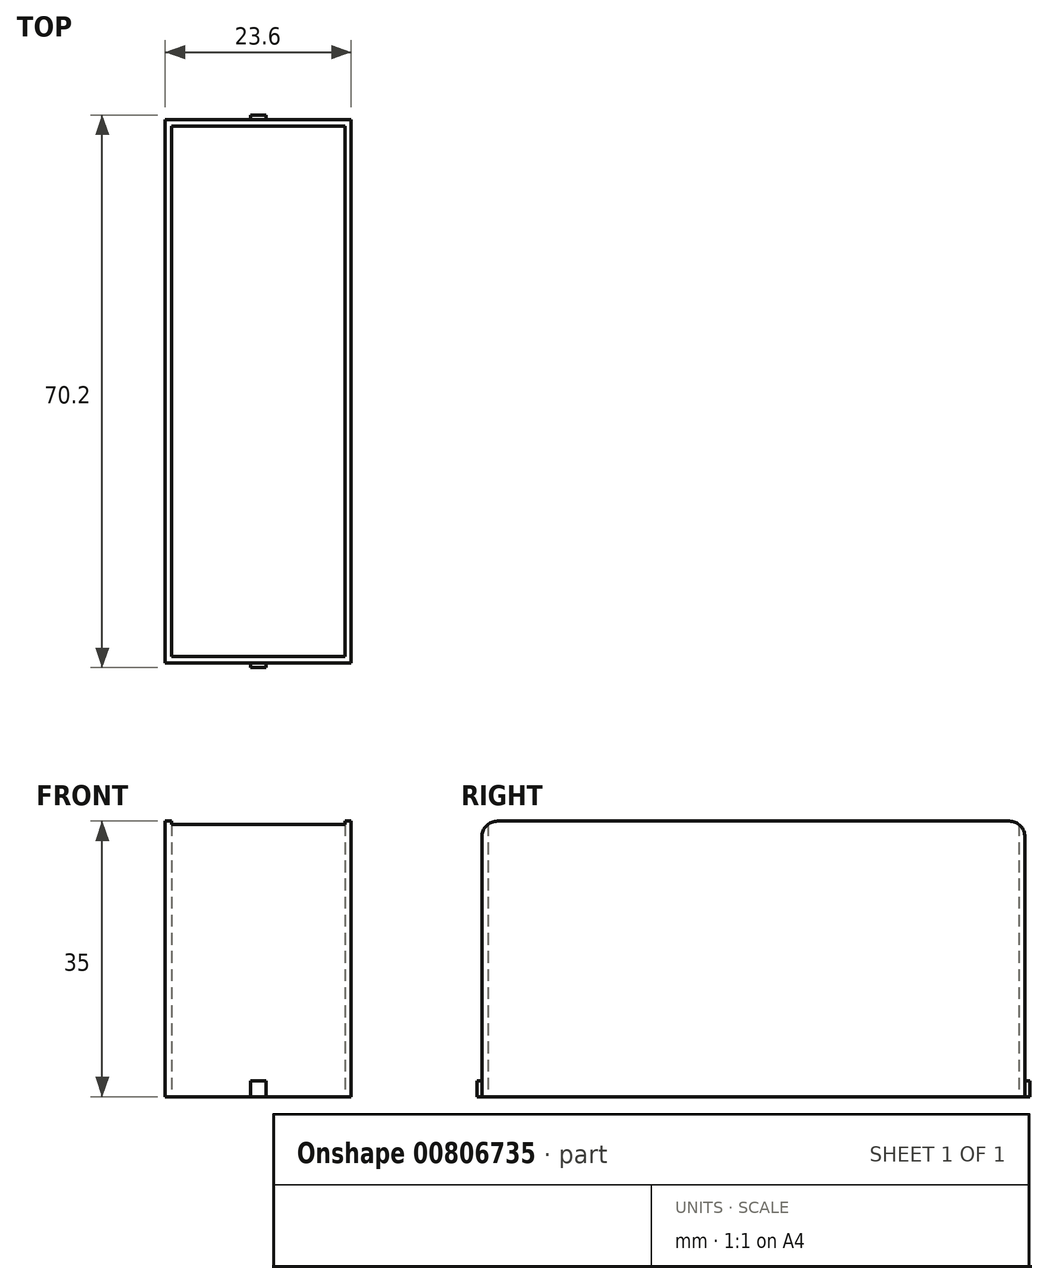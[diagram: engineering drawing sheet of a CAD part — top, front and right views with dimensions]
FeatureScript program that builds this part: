
annotation { "Feature Type Name" : "Feature", "Feature Type Description" : "" }
export const myFeature = defineFeature(function(context is Context, id is Id, definition is map)
    precondition{}
    {
        {
            var Q0;
            Q0=qCreatedBy(makeId("Top.planeOp"),FACE);
            var sketch = newSketch(context, id + "F0", { "sketchPlane" : qUnion([Q0])});
            skLineSegment(sketch, "E0.bottom", {"start": v(-11, 33.7) * mm, "end": v(11, 33.7) * mm});
            skLineSegment(sketch, "E0.top", {"start": v(-11, -33.7) * mm, "end": v(11, -33.7) * mm});
            skLineSegment(sketch, "E0.left", {"start": v(-11, 33.7) * mm, "end": v(-11, -33.7) * mm});
            skLineSegment(sketch, "E0.right", {"start": v(11, 33.7) * mm, "end": v(11, -33.7) * mm});
            skLineSegment(sketch, "E1.bottom", {"start": v(-11.8, 34.5) * mm, "end": v(11.8, 34.5) * mm});
            skLineSegment(sketch, "E1.top", {"start": v(-11.8, -34.5) * mm, "end": v(11.8, -34.5) * mm});
            skLineSegment(sketch, "E1.left", {"start": v(-11.8, 34.5) * mm, "end": v(-11.8, -34.5) * mm});
            skLineSegment(sketch, "E1.right", {"start": v(11.8, 34.5) * mm, "end": v(11.8, -34.5) * mm});
            skSolve(sketch);
        }
        {
            var Q0;
            Q0 = qSketchRegion(id + "F0", true);
            extrude(context, id + "F1", {"entities" : qUnion([Q0]), "depth" : 35 * mm, "offsetDistance" : 25 * mm});
        }
        {
            var Q0;
            Q0=makeQuery(id+"F1.opExtrude","CAP_EDGE",EDGE,{"disambiguationData":[OSD([sQuery(id+"F0.wireOp",EDGE,"E1.top")])],"isStart":false});
            var Q1;
            Q1=makeQuery(id+"F1.opExtrude","CAP_EDGE",EDGE,{"disambiguationData":[OSD([sQuery(id+"F0.wireOp",EDGE,"E1.bottom")])],"isStart":false});
            fillet(context, id + "F2", {"entities" : qUnion([Q0, Q1]), "radius" : 2 * mm, "tangentPropagation" : true, "allowEdgeOverflow" : false});
        }
        {
            var Q0;
            Q0=makeQuery(id+"F1.opExtrude","CAP_FACE",FACE,{"disambiguationData":[OSD([sQuery(id+"F0.wireOp",EDGE,"E0.bottom"),sQuery(id+"F0.wireOp",EDGE,"E0.top"),sQuery(id+"F0.wireOp",EDGE,"E0.left"),sQuery(id+"F0.wireOp",EDGE,"E0.right"),sQuery(id+"F0.wireOp",EDGE,"E1.bottom"),sQuery(id+"F0.wireOp",EDGE,"E1.top"),sQuery(id+"F0.wireOp",EDGE,"E1.left"),sQuery(id+"F0.wireOp",EDGE,"E1.right")])],"isStart":true});
            var sketch = newSketch(context, id + "F3", { "sketchPlane" : qUnion([Q0])});
            skLineSegment(sketch, "E2.bottom", {"start": v(-1, 35.1) * mm, "end": v(1, 35.1) * mm});
            skLineSegment(sketch, "E2.top", {"start": v(-1, 34.5) * mm, "end": v(1, 34.5) * mm});
            skLineSegment(sketch, "E2.left", {"start": v(-1, 35.1) * mm, "end": v(-1, 34.5) * mm});
            skLineSegment(sketch, "E2.right", {"start": v(1, 35.1) * mm, "end": v(1, 34.5) * mm});
            skLineSegment(sketch, "E3.bottom", {"start": v(-1, -35.1) * mm, "end": v(1, -35.1) * mm});
            skLineSegment(sketch, "E3.top", {"start": v(-1, -34.5) * mm, "end": v(1, -34.5) * mm});
            skLineSegment(sketch, "E3.left", {"start": v(-1, -35.1) * mm, "end": v(-1, -34.5) * mm});
            skLineSegment(sketch, "E3.right", {"start": v(1, -35.1) * mm, "end": v(1, -34.5) * mm});
            skSolve(sketch);
        }
        {
            var Q0;
            Q0=makeQuery(id+"F3.imprint","IMPRINT",FACE,{"disambiguationData":[TD([[makeQuery(id+"F3.imprint","IMPRINT",EDGE,{"derivedFrom":sQuery(id+"F3.wireOp",EDGE,"E2.bottom")}),-1.0]])]});
            var Q1;
            Q1=makeQuery(id+"F3.imprint","IMPRINT",FACE,{"disambiguationData":[TD([[makeQuery(id+"F3.imprint","IMPRINT",EDGE,{"derivedFrom":sQuery(id+"F3.wireOp",EDGE,"E3.bottom")}),1.0]])]});
            extrude(context, id + "F4", {"entities" : qUnion([Q0, Q1]), "operationType" : NewBodyOperationType.ADD, "oppositeDirection" : true, "depth" : 2 * mm, "offsetDistance" : 25 * mm});
        }
    });
